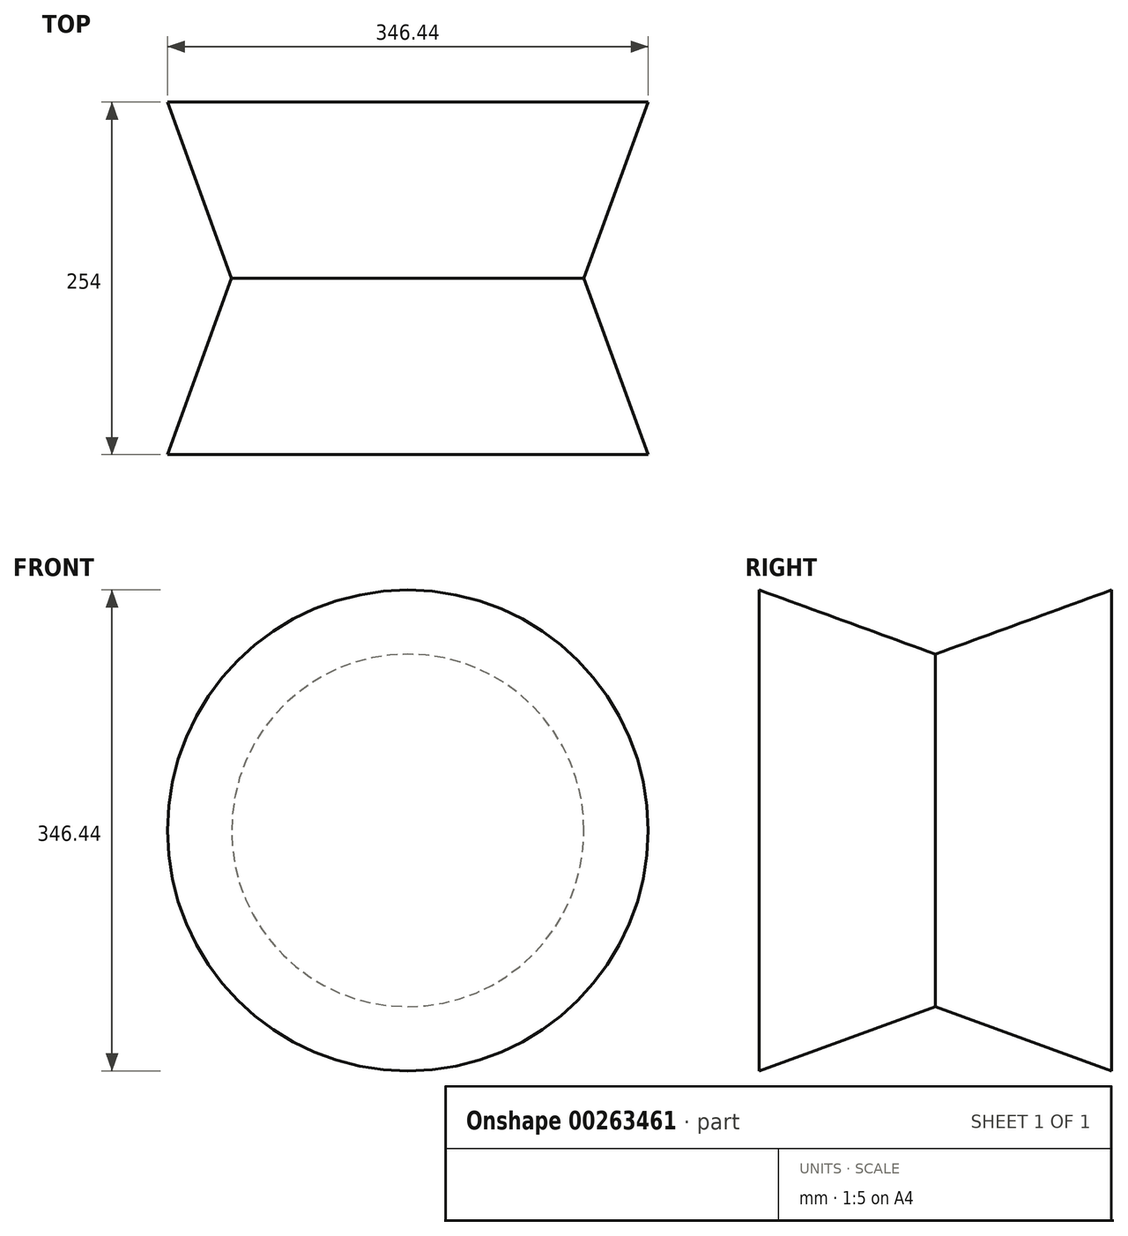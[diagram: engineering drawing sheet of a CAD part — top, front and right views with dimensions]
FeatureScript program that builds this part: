
annotation { "Feature Type Name" : "Feature", "Feature Type Description" : "" }
export const myFeature = defineFeature(function(context is Context, id is Id, definition is map)
    precondition{}
    {
        {
            var Q0;
            Q0=qCreatedBy(makeId("Front.planeOp"),FACE);
            var sketch = newSketch(context, id + "F0", { "sketchPlane" : qUnion([Q0])});
            skCircle(sketch, "E0", {"center": v(0, 0) * mm, "radius": 127 * mm});
            skSolve(sketch);
        }
        {
            var Q0;
            Q0=makeQuery(id+"F0.imprint","IMPRINT",FACE,{"disambiguationData":[TD([[makeQuery(id+"F0.imprint","IMPRINT",EDGE,{"derivedFrom":sQuery(id+"F0.wireOp",EDGE,"E0")}),1.0]])]});
            extrude(context, id + "F1", {"entities" : qUnion([Q0]), "endBound" : BoundingType.SYMMETRIC, "oppositeDirection" : true, "depth" : 254 * mm, "hasDraft" : true, "draftAngle" : 20 * degree});
        }
    });
